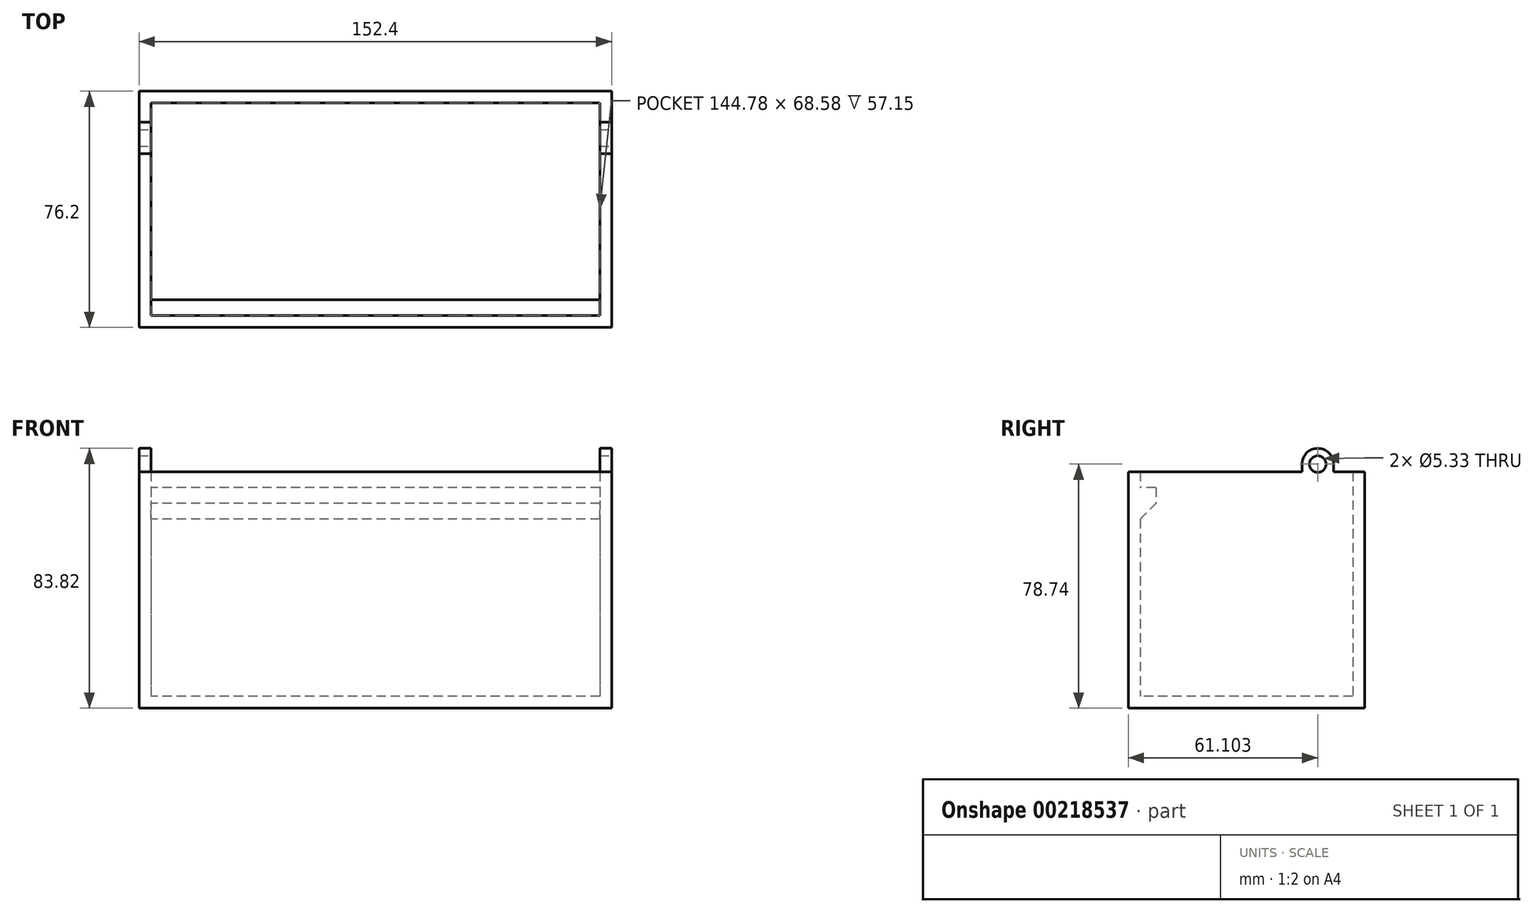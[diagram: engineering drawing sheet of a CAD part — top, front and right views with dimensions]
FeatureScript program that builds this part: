
annotation { "Feature Type Name" : "Feature", "Feature Type Description" : "" }
export const myFeature = defineFeature(function(context is Context, id is Id, definition is map)
    precondition{}
    {
        {
            var Q0;
            Q0=qCreatedBy(makeId("Top.planeOp"),FACE);
            var sketch = newSketch(context, id + "F0", { "sketchPlane" : qUnion([Q0])});
            skLineSegment(sketch, "E0.bottom", {"start": v(76.2, 38.1) * mm, "end": v(-76.2, 38.1) * mm});
            skLineSegment(sketch, "E0.top", {"start": v(76.2, -38.1) * mm, "end": v(-76.2, -38.1) * mm});
            skLineSegment(sketch, "E0.left", {"start": v(76.2, 38.1) * mm, "end": v(76.2, -38.1) * mm});
            skLineSegment(sketch, "E0.right", {"start": v(-76.2, 38.1) * mm, "end": v(-76.2, -38.1) * mm});
            skPoint(sketch, "E0.middle", {"position": v(0, 0) * mm});
            skSolve(sketch);
        }
        {
            var Q0;
            Q0 = qSketchRegion(id + "F0", true);
            extrude(context, id + "F1", {"entities" : qUnion([Q0]), "depth" : 76.2 * mm});
        }
        {
            var Q0;
            Q0=makeQuery(id+"F1.opExtrude","CAP_FACE",FACE,{"disambiguationData":[OSD([sQuery(id+"F0.wireOp",EDGE,"E0.bottom"),sQuery(id+"F0.wireOp",EDGE,"E0.top"),sQuery(id+"F0.wireOp",EDGE,"E0.left"),sQuery(id+"F0.wireOp",EDGE,"E0.right")])],"isStart":false});
            shell(context, id + "F2", {"entities" : qUnion([Q0]), "thickness" : 3.8 * mm});
        }
        {
            var Q0;
            Q0=makeQuery(id+"F1.opExtrude","CAP_FACE",FACE,{"disambiguationData":[OSD([sQuery(id+"F0.wireOp",EDGE,"E0.bottom"),sQuery(id+"F0.wireOp",EDGE,"E0.top"),sQuery(id+"F0.wireOp",EDGE,"E0.left"),sQuery(id+"F0.wireOp",EDGE,"E0.right")])],"isStart":false});
            var sketch = newSketch(context, id + "F3", { "sketchPlane" : qUnion([Q0])});
            skLineSegment(sketch, "E1.bottom", {"start": v(-76.2, 28.08) * mm, "end": v(-72.4, 28.08) * mm});
            skLineSegment(sketch, "E1.top", {"start": v(-76.2, 17.92) * mm, "end": v(-72.4, 17.92) * mm});
            skLineSegment(sketch, "E1.left", {"start": v(-76.2, 28.08) * mm, "end": v(-76.2, 17.92) * mm});
            skLineSegment(sketch, "E1.right", {"start": v(-72.4, 28.08) * mm, "end": v(-72.4, 17.92) * mm});
            skLineSegment(sketch, "E2.MirrorCS", {"start": v(76.2, 17.92) * mm, "end": v(72.4, 17.92) * mm});
            skLineSegment(sketch, "E3.MirrorCS", {"start": v(76.2, 28.08) * mm, "end": v(72.4, 28.08) * mm});
            skLineSegment(sketch, "E4.MirrorCS", {"start": v(76.2, 28.08) * mm, "end": v(76.2, 17.92) * mm});
            skLineSegment(sketch, "E5.MirrorCS", {"start": v(72.4, 28.08) * mm, "end": v(72.4, 17.92) * mm});
            skSolve(sketch);
        }
        {
            var Q0;
            Q0 = qSketchRegion(id + "F3", true);
            extrude(context, id + "F4", {"entities" : qUnion([Q0]), "operationType" : NewBodyOperationType.ADD, "depth" : 7.62 * mm});
        }
        {
            var Q0;
            Q0=makeQuery(id+"F4.boolean.opBoolean","MERGE",FACE,{"derivedFrom":[makeQuery(id+"F1.opExtrude","SWEPT_FACE",FACE,{"disambiguationData":[OSD([sQuery(id+"F0.wireOp",EDGE,"E0.left")])]}),makeQuery(id+"F4.opExtrude","SWEPT_FACE",FACE,{"disambiguationData":[OSD([sQuery(id+"F3.wireOp",EDGE,"E4.MirrorCS")])]})]});
            var sketch = newSketch(context, id + "F5", { "sketchPlane" : qUnion([Q0])});
            skCircle(sketch, "E6", {"center": v(23, 78.74) * mm, "radius": 2.67 * mm});
            skSolve(sketch);
        }
        {
            var Q0;
            Q0 = qSketchRegion(id + "F5", true);
            extrude(context, id + "F6", {"entities" : qUnion([Q0]), "operationType" : NewBodyOperationType.REMOVE, "endBound" : BoundingType.THROUGH_ALL, "oppositeDirection" : true, "depth" : 25.4 * mm});
        }
        {
            var Q0;
            Q0=makeQuery(id+"F4.opExtrude","CAP_EDGE",EDGE,{"disambiguationData":[OSD([sQuery(id+"F3.wireOp",EDGE,"E2.MirrorCS")])],"isStart":false});
            var Q1;
            Q1=makeQuery(id+"F4.opExtrude","CAP_EDGE",EDGE,{"disambiguationData":[OSD([sQuery(id+"F3.wireOp",EDGE,"E3.MirrorCS")])],"isStart":false});
            var Q2;
            Q2=makeQuery(id+"F4.opExtrude","CAP_EDGE",EDGE,{"disambiguationData":[OSD([sQuery(id+"F3.wireOp",EDGE,"E1.bottom")])],"isStart":false});
            var Q3;
            Q3=makeQuery(id+"F4.opExtrude","CAP_EDGE",EDGE,{"disambiguationData":[OSD([sQuery(id+"F3.wireOp",EDGE,"E1.top")])],"isStart":false});
            fillet(context, id + "F7", {"entities" : qUnion([Q0, Q1, Q2, Q3]), "radius" : 5.08 * mm, "tangentPropagation" : true, "allowEdgeOverflow" : false});
        }
        {
            var Q0;
            Q0=makeQuery(id+"F2.opShell","OFFSET_FACE",FACE,{"disambiguationData":[OSD([sQuery(id+"F0.wireOp",EDGE,"E0.top")])]});
            var sketch = newSketch(context, id + "F8", { "sketchPlane" : qUnion([Q0])});
            skLineSegment(sketch, "E7.bottom", {"start": v(-72.4, 71.12) * mm, "end": v(72.4, 71.12) * mm});
            skLineSegment(sketch, "E7.top", {"start": v(-72.4, 66.04) * mm, "end": v(72.4, 66.04) * mm});
            skLineSegment(sketch, "E7.left", {"start": v(-72.4, 71.12) * mm, "end": v(-72.4, 66.04) * mm});
            skLineSegment(sketch, "E7.right", {"start": v(72.4, 71.12) * mm, "end": v(72.4, 66.04) * mm});
            skSolve(sketch);
        }
        {
            var Q0;
            Q0 = qSketchRegion(id + "F8", true);
            extrude(context, id + "F9", {"entities" : qUnion([Q0]), "operationType" : NewBodyOperationType.ADD, "depth" : 5.08 * mm});
        }
        {
            var Q0;
            Q0=makeQuery(id+"F4.boolean.opBoolean","MERGE",FACE,{"derivedFrom":[makeQuery(id+"F2.opShell","OFFSET_FACE",FACE,{"disambiguationData":[OSD([sQuery(id+"F0.wireOp",EDGE,"E0.right")])]}),makeQuery(id+"F4.opExtrude","SWEPT_FACE",FACE,{"disambiguationData":[OSD([sQuery(id+"F3.wireOp",EDGE,"E1.right")])]})]});
            var sketch = newSketch(context, id + "F10", { "sketchPlane" : qUnion([Q0])});
            skLineSegment(sketch, "E8", {"start": v(-29.21, 66.04) * mm, "end": v(-34.3, 66.04) * mm});
            skLineSegment(sketch, "E9", {"start": v(-34.3, 66.04) * mm, "end": v(-34.3, 60.96) * mm});
            skLineSegment(sketch, "E10", {"start": v(-34.3, 60.96) * mm, "end": v(-29.21, 66.04) * mm});
            skSolve(sketch);
        }
        {
            var Q0;
            Q0 = qSketchRegion(id + "F10", true);
            extrude(context, id + "F11", {"entities" : qUnion([Q0]), "operationType" : NewBodyOperationType.ADD, "depth" : 144.78 * mm});
        }
    });
